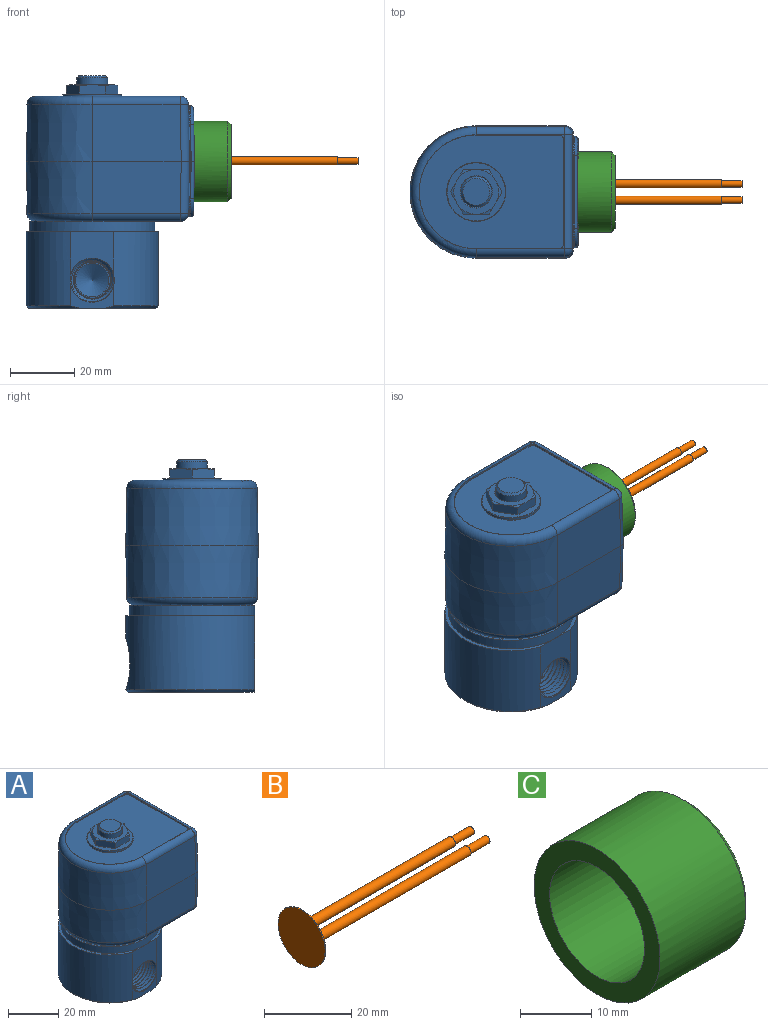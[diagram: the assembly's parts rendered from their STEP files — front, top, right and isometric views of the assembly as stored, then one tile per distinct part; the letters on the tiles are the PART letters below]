
ASSEMBLY  parts=3 mates=2
PART A: 160 faces, bbox 54.2x44.4x72.7 mm
  f0: cylinder r=6.86mm len=13.33mm, axis (0,-1,0), area 0.4mm2, adj f2,f132,f134
  f1: plane 41.06x39.97mm, normal (0,0,1), area 128.2mm2, adj f2,f3,f130
  f2: cylinder r=20.53mm len=41.06mm, axis (0,0,-1), area 2475.9mm2, adj f0,f1,f3,f131,f132,f133,f134,f135
  f3: plane 13.22x13.21mm, normal (0,-1,0), area 125.8mm2, adj f1,f2,f133
  f4: plane 8.33x8.33mm, normal (0,0,1), area 54.5mm2, adj f6
  f5: plane 8.59x8.59mm, normal (1,0,0), area 57.9mm2, adj f7
  f6: cone r=4.8mm half-angle=45deg, axis (0,0,-1), area 25.3mm2, adj f4,f8
  f7: cylinder r=4.29mm len=8.59mm, axis (-1,0,0), area 1.4mm2, adj f5,f9
  f8: cylinder r=4.8mm len=9.6mm, axis (0,0,-1), area 72.1mm2, adj f6,f10
  f9: torus R=5.82mm, axis (1,0,0), area 72.9mm2, adj f7,f11
  f10: cone r=5.02mm half-angle=45deg, axis (0,0,1), area 9.4mm2, adj f8,f17
  f11: plane 15.36x15.36mm, normal (1,0,0), area 75mm2, adj f9,f19
  f12: cone r=8mm half-angle=75deg, axis (0,0,-1), area 3.1mm2, adj f17,f21,f23
  f13: cone r=8mm half-angle=75deg, axis (0,0,-1), area 3.1mm2, adj f17,f23,f25
  f14: cone r=8mm half-angle=75deg, axis (0,0,-1), area 3.1mm2, adj f17,f25,f27
  f15: cone r=8mm half-angle=75deg, axis (0,0,-1), area 3.1mm2, adj f17,f27,f29
  f16: cone r=8mm half-angle=75deg, axis (0,0,-1), area 3.1mm2, adj f17,f29,f31
  f17: plane 13.95x13.84mm, normal (0,0,1), area 73.5mm2, adj f10,f12,f13,f14,f15,f16,f18,f21
  f18: cone r=8mm half-angle=75deg, axis (0,0,-1), area 3.1mm2, adj f17,f21,f31
  f19: cylinder r=7.59mm len=15.19mm, axis (1,0,0), area 75.1mm2, adj f11,f32
  f20: cone r=8mm half-angle=75deg, axis (0,0,1), area 0.6mm2, adj f21,f31,f33
  f21: plane 8.36x3.42mm, normal (0,1,0), area 23.5mm2, adj f12,f17,f18,f20,f22,f23,f31,f33
  f22: cone r=8mm half-angle=75deg, axis (0,0,1), area 0.6mm2, adj f21,f23,f33
  f23: plane 7.29x4.36mm, normal (0.87,0.5,0), area 23.5mm2, adj f12,f13,f17,f21,f22,f24,f25,f33
  f24: cone r=8mm half-angle=75deg, axis (0,0,1), area 0.6mm2, adj f23,f25,f33
  f25: plane 7.29x4.36mm, normal (0.87,-0.5,0), area 23.5mm2, adj f13,f14,f17,f23,f24,f26,f27,f33
  f26: cone r=8mm half-angle=75deg, axis (0,0,1), area 0.6mm2, adj f25,f27,f33
  f27: plane 8.36x3.42mm, normal (0,-1,0), area 23.5mm2, adj f14,f15,f17,f25,f26,f28,f29,f33
  f28: cone r=8mm half-angle=75deg, axis (0,0,1), area 0.6mm2, adj f27,f29,f33
  f29: plane 7.29x4.36mm, normal (-0.87,-0.5,0), area 23.5mm2, adj f15,f16,f17,f27,f28,f30,f31,f33
  f30: cone r=8mm half-angle=75deg, axis (0,0,1), area 0.6mm2, adj f29,f31,f33
  f31: plane 7.29x4.36mm, normal (-0.87,0.5,0), area 23.5mm2, adj f16,f17,f18,f20,f21,f29,f30,f33
  f32: plane 25.4x25.4mm, normal (1,0,0), area 325.5mm2, adj f19,f34
  f33: plane 18.05x18.05mm, normal (0,0,1), area 92.5mm2, adj f20,f21,f22,f23,f24,f25,f26,f27
  f34: cylinder r=12.7mm len=25.4mm, axis (-1,0,0), area 178.4mm2, adj f32,f36
  f35: torus R=9.02mm, axis (0,0,1), area 11.4mm2, adj f33,f37
  f36: plane 29.41x29.41mm, normal (1,0,0), area 318.1mm2, adj f34,f38,f39,f40,f41,f42,f43,f44
  f37: cylinder r=9.15mm len=18.3mm, axis (0,0,-1), area 42.9mm2, adj f35,f50
  f38: plane 23.06x1.57mm, normal (0,1,0), area 36.3mm2, adj f36,f39,f45,f56
  f39: cylinder r=3.17mm len=3.18mm, axis (-1,0,0), area 7.9mm2, adj f36,f38,f40,f56
  f40: plane 23.06x1.57mm, normal (0,0,1), area 36.3mm2, adj f36,f39,f41,f56
  f41: cylinder r=3.17mm len=3.18mm, axis (-1,0,0), area 7.9mm2, adj f36,f40,f42,f56
  f42: plane 23.06x1.57mm, normal (0,-1,0), area 36.3mm2, adj f36,f41,f43,f56
  f43: cylinder r=3.17mm len=3.18mm, axis (-1,0,0), area 7.9mm2, adj f36,f42,f44,f56
  f44: plane 23.06x1.57mm, normal (0,0,-1), area 36.3mm2, adj f36,f43,f45,f56
  f45: cylinder r=3.17mm len=3.18mm, axis (-1,0,0), area 7.9mm2, adj f36,f38,f44,f56
  f46: cylinder r=1.59mm len=3.18mm, axis (-1,0,0), area 15.7mm2, adj f36,f56
  f47: cylinder r=1.59mm len=3.18mm, axis (-1,0,0), area 15.7mm2, adj f36,f56
  f48: cylinder r=1.59mm len=3.18mm, axis (-1,0,0), area 15.7mm2, adj f36,f56
  f49: cylinder r=1.59mm len=3.18mm, axis (-1,0,0), area 15.7mm2, adj f36,f56
  f50: torus R=9.02mm, axis (0,0,1), area 11.4mm2, adj f37,f57
  f51: cylinder r=1.02mm len=11.51mm, axis (-0.02,-0.02,1), area 18.4mm2, adj f52,f61,f64,f80
  f52: bspline ~6x5.9mm, area 13.5mm2, adj f51,f53,f60,f64
  f53: cylinder r=1.02mm len=22.41mm, axis (0,-1,0), area 35.4mm2, adj f52,f54,f59,f64
  f54: bspline ~6x5.9mm, area 13.5mm2, adj f53,f55,f58,f64
  f55: cylinder r=1.02mm len=11.51mm, axis (0.02,-0.02,-1), area 18.4mm2, adj f54,f62,f64,f78
  f56: plane 29.41x29.41mm, normal (-1,0,0), area 308.9mm2, adj f38,f39,f40,f41,f42,f43,f44,f45
  f57: plane 44.83x35.31mm, normal (0,0,1), area 1192.3mm2, adj f50,f66,f67,f68,f69,f70,f71
  f58: cylinder r=5.84mm len=5.84mm, axis (-1,0,0), area 1.8mm2, adj f54,f59,f62,f72
  f59: plane 22.41x0.2mm, normal (0,0,1), area 4.5mm2, adj f53,f58,f60,f73
  f60: cylinder r=5.84mm len=5.84mm, axis (-1,0,0), area 1.8mm2, adj f52,f59,f61,f74
  f61: plane 11.51x0.38mm, normal (0,1,0.02), area 2mm2, adj f51,f60,f75,f89
  f62: plane 11.51x0.38mm, normal (0,-1,0.02), area 2mm2, adj f55,f58,f77,f87
  f63: cylinder r=12.7mm len=21.82mm, axis (-1,0,0), area 52.3mm2, adj f56,f65,f81
  f64: plane 32.91x16.7mm, normal (1,0,0.02), area 254mm2, adj f51,f52,f53,f54,f55,f65,f81
  f65: cone r=12.81mm half-angle=1deg, axis (-1,0,0), area 172.7mm2, adj f56,f63,f64,f81
  f66: plane 25.53x0.51mm, normal (0,-1,0), area 13mm2, adj f57,f67,f71,f82
  f67: cylinder r=1.65mm len=1.65mm, axis (0,0,-1), area 1.3mm2, adj f57,f66,f68,f82
  f68: plane 32x0.51mm, normal (-1,0,0), area 16.3mm2, adj f57,f67,f69,f82
  f69: cylinder r=1.65mm len=1.65mm, axis (0,0,-1), area 1.3mm2, adj f57,f68,f70,f82
  f70: plane 25.53x0.51mm, normal (0,1,0), area 13mm2, adj f57,f69,f71,f82
  f71: cylinder r=17.65mm len=35.31mm, axis (0,0,1), area 28.2mm2, adj f57,f66,f70,f82
  f72: revolved ~6.22x6.12mm, area 5.5mm2, adj f58,f73,f77,f84
  f73: cylinder r=0.38mm len=22.41mm, axis (0,-1,0), area 13.3mm2, adj f59,f72,f74,f84
  f74: revolved ~6.22x6.12mm, area 5.5mm2, adj f60,f73,f75,f84
  f75: cylinder r=0.38mm len=11.51mm, axis (-0.02,-0.02,1), area 6.9mm2, adj f61,f74,f84,f100
  f76: cylinder r=2.54mm len=35.4mm, axis (0,1,0), area 139.7mm2, adj f79,f82,f83,f84
  f77: cylinder r=0.38mm len=11.51mm, axis (0.02,-0.02,-1), area 6.9mm2, adj f62,f72,f84,f97
  f78: cylinder r=1.02mm len=11.51mm, axis (-0.02,0.02,-1), area 18.4mm2, adj f55,f81,f87,f92
  f79: sphere r=2.54mm, area 6.3mm2, adj f76,f86,f88
  f80: cylinder r=1.02mm len=11.51mm, axis (0.02,0.02,1), area 18.4mm2, adj f51,f81,f89,f90
  f81: plane 32.68x16.46mm, normal (1,0,-0.02), area 259.5mm2, adj f63,f64,f65,f78,f80,f90,f91,f92
  f82: plane 45.52x35.92mm, normal (0,0,1), area 12.5mm2, adj f66,f67,f68,f69,f70,f71,f76,f85
  f83: sphere r=2.54mm, area 6.3mm2, adj f76,f93,f94
  f84: plane 36.21x17.91mm, normal (1,0,0.02), area 33.1mm2, adj f72,f73,f74,f75,f76,f77,f88,f94
  f85: torus R=17.7mm, axis (0,0,1), area 239.3mm2, adj f82,f86,f93,f95
  f86: cylinder r=2.54mm len=27.3mm, axis (1,0,0), area 107.7mm2, adj f79,f82,f85,f96
  f87: plane 11.51x0.38mm, normal (0,-1,-0.02), area 2mm2, adj f62,f78,f97,f104
  f88: cylinder r=2.54mm len=17.74mm, axis (0.02,-0.02,-1), area 70.7mm2, adj f79,f84,f96,f99
  f89: plane 11.51x0.38mm, normal (0,1,-0.02), area 2mm2, adj f61,f80,f100,f102
  f90: bspline ~6x5.9mm, area 13.5mm2, adj f80,f81,f91,f102
  f91: cylinder r=1.02mm len=22.41mm, axis (0,1,0), area 35.4mm2, adj f81,f90,f92,f103
  f92: bspline ~6x5.9mm, area 13.5mm2, adj f78,f81,f91,f104
  f93: cylinder r=2.54mm len=27.3mm, axis (-1,0,0), area 107.7mm2, adj f82,f83,f85,f105
  f94: cylinder r=2.54mm len=17.74mm, axis (0.02,0.02,-1), area 70.7mm2, adj f83,f84,f105,f106
  f95: cone r=20.55mm half-angle=1deg, axis (0,0,-1), area 1135.7mm2, adj f85,f96,f105,f109
  f96: plane 27.61x17.72mm, normal (0,-1,0.02), area 486.7mm2, adj f86,f88,f95,f110
  f97: cylinder r=0.38mm len=11.51mm, axis (-0.02,0.02,-1), area 6.9mm2, adj f77,f87,f98,f111
  f98: revolved ~4.64x2.45mm, area 3mm2, adj f97,f104,f111,f116
  f99: cylinder r=2.54mm len=16.17mm, axis (-0.02,0.02,-1), area 64.4mm2, adj f88,f110,f111,f112
  f100: cylinder r=0.38mm len=11.51mm, axis (0.02,0.02,1), area 6.9mm2, adj f75,f89,f101,f113
  f101: revolved ~4.64x2.45mm, area 3mm2, adj f100,f102,f113,f114
  f102: cylinder r=5.84mm len=5.84mm, axis (-1,0,0), area 2.6mm2, adj f89,f90,f101,f103,f114
  f103: plane 22.41x0.61mm, normal (0,0,-1), area 13.6mm2, adj f91,f102,f104,f115
  f104: cylinder r=5.84mm len=5.84mm, axis (-1,0,0), area 2.6mm2, adj f87,f92,f98,f103,f116
  f105: plane 27.61x17.72mm, normal (0,1,0.02), area 486.7mm2, adj f93,f94,f95,f117
  f106: cylinder r=2.54mm len=16.17mm, axis (-0.02,-0.02,-1), area 64.4mm2, adj f94,f113,f117,f118
  f107: cone r=1.98mm half-angle=59deg, axis (0,0,-1), area 14.4mm2, adj f119
  f108: cone r=1.98mm half-angle=59deg, axis (0,0,-1), area 14.4mm2, adj f120
  f109: cone r=20.55mm half-angle=1deg, axis (0,0,1), area 1035.4mm2, adj f95,f110,f117,f121
  f110: plane 27.61x16.15mm, normal (0,-1,-0.02), area 443.6mm2, adj f96,f99,f109,f122
  f111: plane 16.19x2.82mm, normal (1,0,-0.02), area 9.2mm2, adj f84,f97,f98,f99,f123
  f112: sphere r=2.54mm, area 6.3mm2, adj f99,f122,f123
  f113: plane 16.19x2.82mm, normal (1,0,-0.02), area 9.2mm2, adj f84,f100,f101,f106,f123
  f114: bspline ~4.16x1.88mm, area 2.1mm2, adj f101,f102,f115,f123
  f115: cylinder r=0.38mm len=22.41mm, axis (0,-1,0), area 8.7mm2, adj f103,f114,f116,f123
  f116: bspline ~4.16x1.88mm, area 2.1mm2, adj f98,f104,f115,f123
  f117: plane 27.61x16.15mm, normal (0,1,-0.02), area 443.6mm2, adj f105,f106,f109,f124
  f118: sphere r=2.54mm, area 6.3mm2, adj f106,f123,f124
  f119: cylinder r=1.98mm len=10.72mm, axis (0,0,1), area 133.4mm2, adj f107,f125
  f120: cylinder r=1.98mm len=10.72mm, axis (0,0,1), area 133.4mm2, adj f108,f126
  f121: torus R=17.73mm, axis (0,0,1), area 239.6mm2, adj f109,f122,f124,f127
  f122: cylinder r=2.54mm len=27.33mm, axis (-1,0,0), area 107.8mm2, adj f110,f112,f121,f127,f128
  f123: cylinder r=2.54mm len=35.45mm, axis (0,-1,0), area 104.2mm2, adj f111,f112,f113,f114,f115,f116,f118,f128
  f124: cylinder r=2.54mm len=27.33mm, axis (1,0,0), area 107.8mm2, adj f117,f118,f121,f127,f128
  f125: cone r=2.36mm half-angle=45deg, axis (0,0,-1), area 7.4mm2, adj f119,f129
  f126: cone r=2.36mm half-angle=45deg, axis (0,0,-1), area 7.4mm2, adj f120,f129
  f127: plane 39.38x27.91mm, normal (0,0,1), area 117.8mm2, adj f121,f122,f124,f130
  f128: plane 35.45x19.37mm, normal (0,0,-1), area 394.1mm2, adj f122,f123,f124,f130
  f129: plane 39.54x39.21mm, normal (0,0,-1), area 1190.9mm2, adj f125,f126,f131,f132
  f130: cylinder r=19.43mm len=38.86mm, axis (0,0,1), area 387.6mm2, adj f1,f127,f128
  f131: cone r=20.53mm half-angle=45deg, axis (0,0,1), area 125.3mm2, adj f2,f129,f132,f144
  f132: plane 13.37x7.06mm, normal (0,-1,0), area 40.1mm2, adj f0,f2,f129,f131
  f133: cylinder r=6.86mm len=13.33mm, axis (0,-1,0), area 0.4mm2, adj f2,f3,f134
  f134: cone r=6.91mm half-angle=48deg, axis (0,-1,0), area 27.3mm2, adj f0,f2,f133,f135,f136,f137,f138,f139
  f135: cone r=6.86mm half-angle=1.8deg, axis (0,-1,0), area 35.6mm2, adj f2,f134,f136,f138,f140
  f136: bspline ~13.72x13.7mm, area 2.6mm2, adj f134,f135,f137,f140
  f137: bspline ~13.7x13.69mm, area 270.6mm2, adj f134,f136,f139,f140,f143
  f138: bspline ~13.92x13.89mm, area 296.1mm2, adj f134,f135,f139,f140,f143
  f139: bspline ~11.77x11.75mm, area 41.8mm2, adj f134,f137,f138,f143
  f140: cone r=5.5mm half-angle=10deg, axis (0,-1,0), area 8.7mm2, adj f135,f136,f137,f138,f143
  f141: cone r=5.17mm half-angle=59deg, axis (0,-1,0), area 97.9mm2, adj f142
  f142: cylinder r=5.17mm len=10.34mm, axis (0,1,0), area 13.2mm2, adj f141,f143
  f143: plane 12.52x12.43mm, normal (0,-1,0), area 30.4mm2, adj f137,f138,f139,f140,f142
  f144: cone r=10.32mm half-angle=35.5deg, axis (0,1,0), area 84mm2, adj f2,f131,f145,f157,f158,f159
  f145: cone r=10.32mm half-angle=35.5deg, axis (0,1,0), area 14.3mm2, adj f144,f155,f156,f158
  f146: plane 13.72x13.72mm, normal (0,1,0), area 147.8mm2, adj f147
  f147: cylinder r=6.86mm len=13.72mm, axis (0,-1,0), area 35.6mm2, adj f146,f148
  f148: plane 13.72x13.72mm, normal (0,-1,0), area 52.7mm2, adj f147,f153
  f149: cone r=5.5mm half-angle=10deg, axis (0,1,0), area 6.6mm2, adj f150,f156,f157,f158,f159
  f150: cone r=5.5mm half-angle=10deg, axis (0,1,0), area 17.2mm2, adj f149,f151,f156,f158
  f151: cone r=5.5mm half-angle=10deg, axis (0,1,0), area 25.7mm2, adj f150,f152,f156,f158
  f152: cone r=5.5mm half-angle=10deg, axis (0,1,0), area 33.5mm2, adj f151,f153,f156,f158
  f153: cone r=5.5mm half-angle=10deg, axis (0,1,0), area 25.9mm2, adj f148,f152,f154,f156,f158
  f154: plane 6.21x2.4mm, normal (0,-1,0), area 0.5mm2, adj f153,f155,f156,f158
  f155: bspline ~12.08x11.63mm, area 51.4mm2, adj f145,f154,f156,f158
  f156: bspline ~13.81x13.79mm, area 293.3mm2, adj f145,f149,f150,f151,f152,f153,f154,f155
  f157: bspline ~13.59x13.56mm, area 2.2mm2, adj f144,f149,f158,f159
  f158: bspline ~14.11x13.57mm, area 278.9mm2, adj f144,f145,f149,f150,f151,f152,f153,f154
  f159: cone r=6.86mm half-angle=1.8deg, axis (0,1,0), area 30.4mm2, adj f144,f149,f156,f157
PART B: 11 faces, bbox 57.4x15.2x15.2 mm
  f0: plane 2.03x2.03mm, normal (1,0,0), area 3.2mm2, adj f1
  f1: cylinder r=1.02mm len=6.35mm, axis (1,0,0), area 40.5mm2, adj f0,f4
  f2: plane 2.03x2.03mm, normal (1,0,0), area 3.2mm2, adj f5
  f3: plane 15.24x15.24mm, normal (-1,0,0), area 182.4mm2, adj f6
  f4: plane 2.54x2.54mm, normal (1,0,0), area 1.8mm2, adj f1,f7
  f5: cylinder r=1.02mm len=6.35mm, axis (1,0,0), area 40.5mm2, adj f2,f8
  f6: cylinder r=7.62mm len=15.24mm, axis (1,0,0), area 12.2mm2, adj f3,f9
  f7: cylinder r=1.27mm len=50.8mm, axis (1,0,0), area 405.4mm2, adj f4,f9
  f8: plane 2.54x2.54mm, normal (1,0,0), area 1.8mm2, adj f5,f10
  f9: plane 15.24x15.24mm, normal (1,0,0), area 172.3mm2, adj f6,f7,f10
  f10: cylinder r=1.27mm len=50.8mm, axis (1,0,0), area 405.4mm2, adj f8,f9
PART C: 6 faces, bbox 18x24.9x24.9 mm
  f0: cone r=10.41mm half-angle=45deg, axis (1,0,0), area 89.4mm2, adj f1,f2
  f1: cylinder r=9.4mm len=18.8mm, axis (1,0,0), area 1003.4mm2, adj f0,f3
  f2: plane 22.91x22.91mm, normal (1,0,0), area 71.5mm2, adj f0,f4
  f3: plane 24.94x24.94mm, normal (-1,0,0), area 211.2mm2, adj f1,f5
  f4: cone r=12.47mm half-angle=45deg, axis (-1,0,0), area 108mm2, adj f2,f5
  f5: cylinder r=12.47mm len=24.94mm, axis (1,0,0), area 1331.5mm2, adj f3,f4
PLACE A t=(-18.63,65.1,12.88)mm
PLACE B t=(-24.98,65.1,12.88)mm
PLACE C t=(-24.98,65.1,12.68)mm
MATE fastened C.f1 <-> A.f5  axis (-1,0,0) through (6.44,65.1,49.69)mm
MATE fastened B.f6 <-> A.f7  axis (-1,0,0) through (6.44,65.1,49.88)mm
